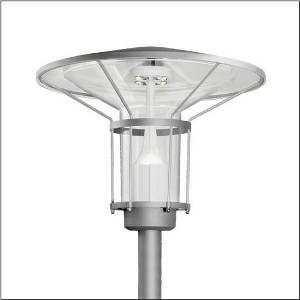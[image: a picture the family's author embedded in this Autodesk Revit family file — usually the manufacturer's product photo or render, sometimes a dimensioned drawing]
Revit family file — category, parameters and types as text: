
# Revit family: laterne_classic_iq___p1_0a_5xa5245bf14h_da05
name_source: partatom
category: Lighting Fixtures
units: mm (PartAtom-declared; Revit-internal decimal feet)

## family parameters
Cut with Voids When Loaded = No
Host = Face
Light Source = No
Part Type = Normal
Room Calculation Point = No
Round Connector Dimension = Use Diameter
Shared = No

## types (1)
- --- (1 x LED, 1360 lm, 12.9 W, 2200K)
    Apparent Load = 13 VA
    CIE Flux Codes = 30 61 91 96 100
    Color Rendering = 70
    Color Temperature = 2200K
    Default Elevation = 1800 mm
    Description = Lantern Classic iQ, mast luminaire, Module 540 iQ-SR, primary light control with 3 zone facetted reflector, of plastic, silver coated, highly specular, structured, primary optical cover: cover, of PMMA, transparent, light distribution: P1.0a, light emission: direct distribution, primary light characteristic: strongly asymmetric, installation type: post-top, LED, High Power LED, rated luminous flux: 1.360lm, luminous efficacy: 105lm/W, light colour: 722, colour temperature: 2200K, control gear: iQ Street-Remote, control: pre-setting: logarithmic dimming characteristic, Street-Remote, Auto-Match, Temp-Guard, Lumen-Switch, Night-Set, Smart-Wire, Light-Fading, Desk-Remote (wireless, voltage-free reading and setting of iQ features in the workshop via application-optimized NFC function/RFID function), optimised constant luminous flux control (CLO 2.0), with terminal, 6-pole, max. 2.5mm², mains connection: 230..240V, AC, 50/60Hz, start of lifetime: 13W, end of service life: 13W, reduction: 6W, luminaire housing, upper part, of glass-fibre reinforced polyester, coated, Siteco® metallic grey (DB 702S), diameter: 750mm, height: 596mm, spigot size: d x l = 76 x 70mm (post-top) | with reducer (optional accessory) 60 x 70mm, mounting height: 3..5m, post-top mast mounting element, of diecast aluminium, coated, Siteco® metallic grey (DB 702S), Module 540 iQ-SR, traffic white (RAL 9016), equipment: standard, protection rating (complete): IP65, insulation class (complete): insulation class II (safety insulation), certification: CE, ENEC, VDE, packaging unit: 1 piece

Light Distribution: P1.0a
    Height = 596 mm
    Lamp = 1 x LED
    Lamp Light Flux = 1360 lm
    Lamp Power = 12.9 W
    Lamp count = 1
    Length = 750 mm
    Luminous efficacy = 105 lm/W
    Manufacturer = Siteco
    ModVariant = No
    Model = 5XA5245BF14H
    Number of Poles = 1
    OnlyDefault = Yes
    Power Factor = 1
    Product Name = Laterne Classic iQ | P1.0a
    Product group = mast luminaire | pylon top
    ProductGroupID = 6100
    Protection Class = Protection class II
    Protection Degree = IP 65
    RLX_Detail_Level = 1
    RLX_Emergency_Light_Flux = 0 lm
    RLX_Emergency_Type = 0
    RLX_Emergency_Type_DB = No
    RlxData = <blob elided: 69321 chars, md5=eb5a2f2d>
    Socket = socket
    Standby Power = 0 W
    System Light Flux = 1360 lm
    System Power = 13 W
    Type Comments = factory setting: luminous flux: 100 % | dim-lin: 254 | 516 mA
    Type Image = l_1006052.jpg
    URL = http://relux.com
    VarID = @adj_160302
    Voltage = 0 V
    Weight = 0.00 kg
    Width = 0 mm  [stored 0 ft]

note: [stored X ft] marks values corroborated as IEEE doubles in the binary element streams (Revit-internal decimal feet)

## geometry (parser evidence)
native form markers: Blend x4, Sweep x8
no freeform markers — native parametric forms only
